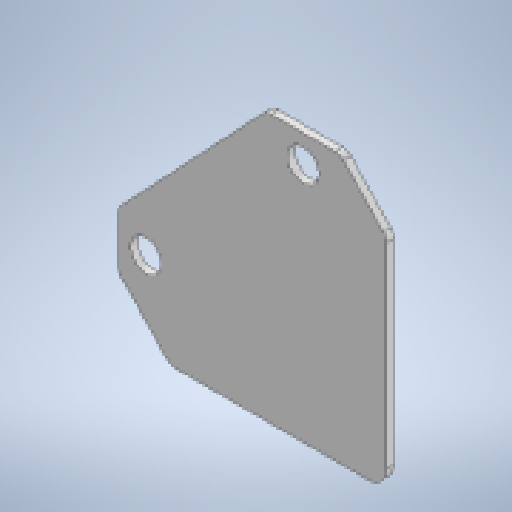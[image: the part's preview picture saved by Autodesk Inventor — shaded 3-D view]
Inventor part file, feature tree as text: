
AUTODESK INVENTOR PART (.ipt)
format: ipt  version: 2025 (Build 290162010, 162A)  size: 202,752 bytes
history: native  units: mm
features: chamfer x2, other x2, sheet_metal_op x1, sketch x1
ambient origin geometry x8: Origin, YZ Plane, XZ Plane, XY Plane, X Axis, Y Axis, Z Axis, Center Point
bodies: Solid1 (feature_tree)
feature tree (6):
  sheet_metal_op  "Face1"
  chamfer  "Corner Round2"
  chamfer  "Corner Round4"
  sketch  "Sketch1"  dims[d2=80.0mm d3=80.0mm d6=4.0mm d17=5.0mm d18=17.0mm d19=45.0mm d20=45.0mm d21=40.0mm d22=15.0mm d23=15.0mm d24=30.0mm d25=6.0mm d26=5.0mm d28=10.0mm]
  other  "Plate1"
  other  "Definition1"
